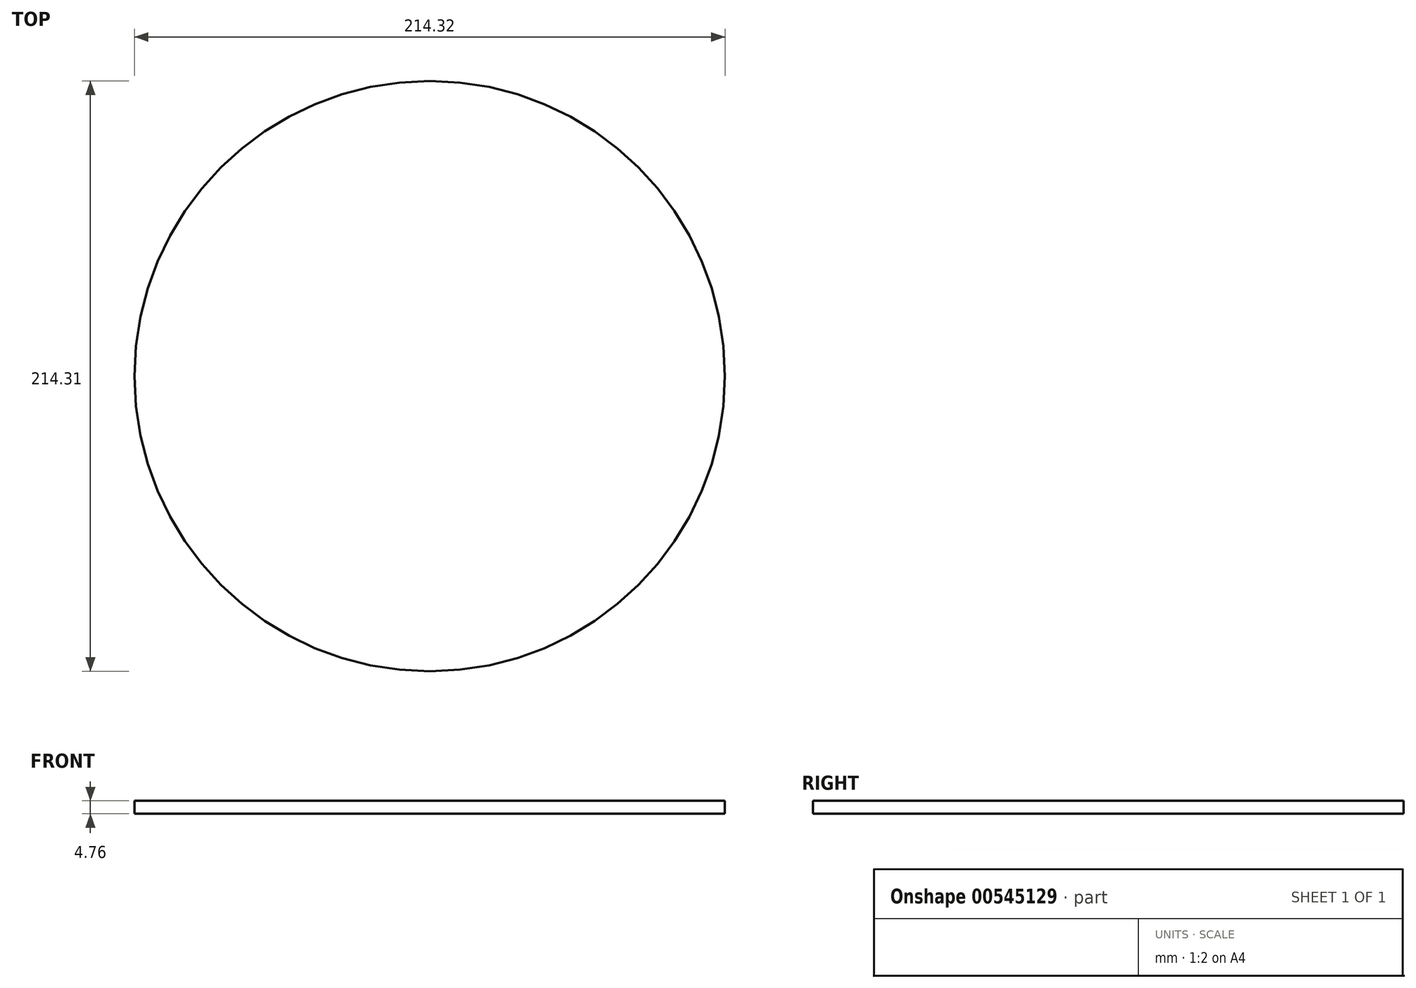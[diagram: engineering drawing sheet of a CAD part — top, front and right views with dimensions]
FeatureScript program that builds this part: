
annotation { "Feature Type Name" : "Feature", "Feature Type Description" : "" }
export const myFeature = defineFeature(function(context is Context, id is Id, definition is map)
    precondition{}
    {
        {
            var Q0;
            Q0=qCreatedBy(makeId("Top.planeOp"),FACE);
            var sketch = newSketch(context, id + "F0", { "sketchPlane" : qUnion([Q0])});
            skCircle(sketch, "E0", {"center": v(0, -4.2) * mm, "radius": 107.16 * mm});
            skSolve(sketch);
        }
        {
            var Q0;
            Q0=makeQuery(id+"F0.imprint","IMPRINT",FACE,{"disambiguationData":[TD([[makeQuery(id+"F0.imprint","IMPRINT",EDGE,{"derivedFrom":sQuery(id+"F0.wireOp",EDGE,"E0")}),1.0]])]});
            extrude(context, id + "F1", {"entities" : qUnion([Q0]), "depth" : 4.76 * mm, "offsetDistance" : 25.4 * mm});
        }
    });
